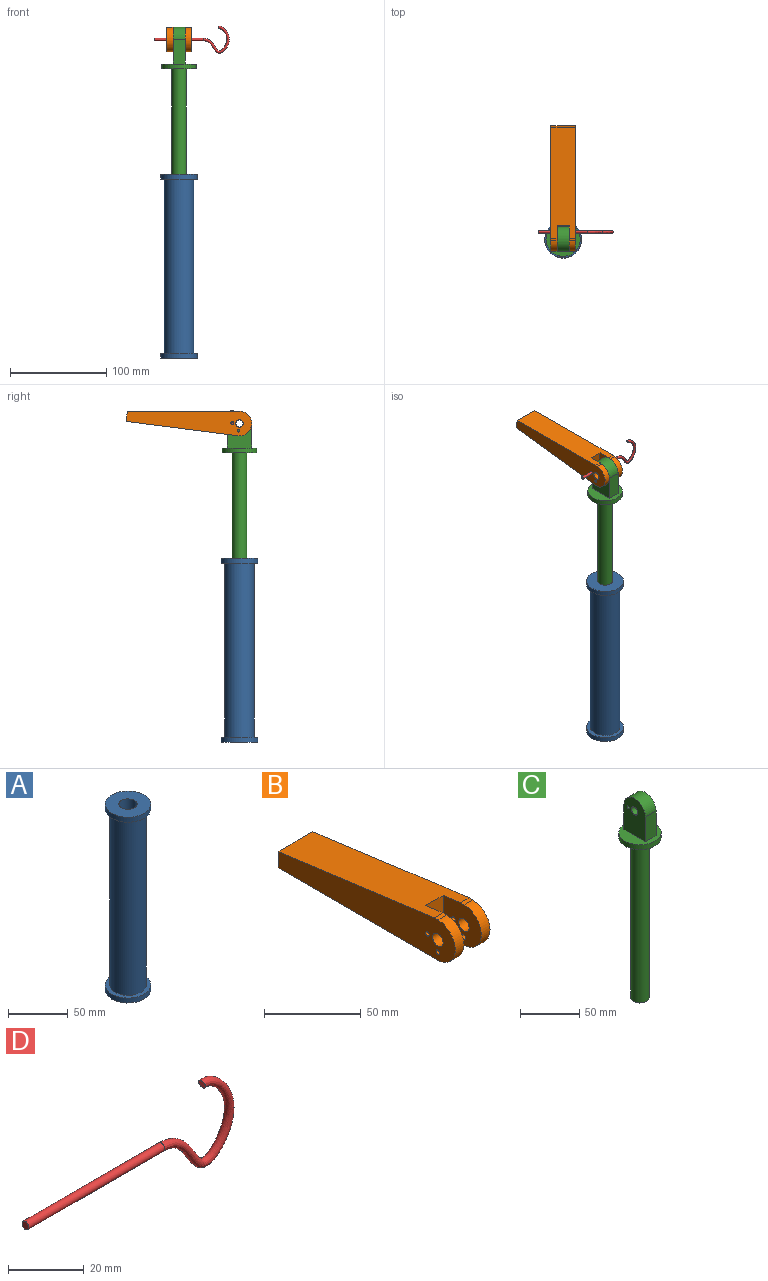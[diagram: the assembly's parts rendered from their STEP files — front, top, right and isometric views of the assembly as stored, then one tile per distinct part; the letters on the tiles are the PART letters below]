
ASSEMBLY  parts=4 mates=3
PART A: 9 faces, bbox 38.1x38.1x190.5 mm
  f0: plane 38.1x38.1mm, normal (0,0,1), area 957.7mm2, adj f1,f8
  f1: cylinder r=7.62mm len=177.8mm, axis (0,0,-1), area 8512.7mm2, adj f0,f2
  f2: plane 15.24x15.24mm, normal (0,0,1), area 182.4mm2, adj f1
  f3: plane 38.1x38.1mm, normal (0,0,-1), area 1140.1mm2, adj f4
  f4: cylinder r=19.05mm len=38.1mm, axis (0,0,-1), area 608mm2, adj f3,f5
  f5: plane 38.1x38.1mm, normal (0,0,1), area 410.4mm2, adj f4,f6
  f6: cylinder r=15.24mm len=180.34mm, axis (0,0,-1), area 17268.6mm2, adj f5,f7
  f7: plane 38.1x38.1mm, normal (0,0,-1), area 410.4mm2, adj f6,f8
  f8: cylinder r=19.05mm len=38.1mm, axis (0,0,-1), area 608mm2, adj f0,f7
PART B: 18 faces, bbox 25.4x129.5x25.4 mm
  f0: plane 6.35x2.54mm, normal (0,0,1), area 16.1mm2, adj f1,f8,f14,f16
  f1: cylinder r=12.7mm len=25.4mm, axis (-1,0,0), area 253.4mm2, adj f0,f2,f14,f16
  f2: plane 116.84x25.4mm, normal (0,0,-1), area 2774.2mm2, adj f1,f6,f7,f13,f14,f15,f16,f17
  f3: cylinder r=3.81mm len=7.62mm, axis (-1,0,0), area 152mm2, adj f14,f16
  f4: cylinder r=1.27mm len=6.35mm, axis (-1,0,0), area 50.7mm2, adj f14,f16
  f5: cylinder r=1.27mm len=6.35mm, axis (-1,0,0), area 50.7mm2, adj f14,f16
  f6: cylinder r=12.7mm len=25.4mm, axis (-1,0,0), area 253.4mm2, adj f2,f12,f13,f17
  f7: plane 25.4x10.16mm, normal (0,1,0), area 258.1mm2, adj f2,f8,f13,f14
  f8: plane 114.3x25.4mm, normal (0,0.13,0.99), area 2766.2mm2, adj f0,f7,f12,f13,f14,f15,f16,f17
  f9: cylinder r=3.81mm len=7.62mm, axis (-1,0,0), area 152mm2, adj f13,f17
  f10: cylinder r=1.27mm len=6.35mm, axis (-1,0,0), area 50.7mm2, adj f13,f17
  f11: cylinder r=1.27mm len=6.35mm, axis (-1,0,0), area 50.7mm2, adj f13,f17
  f12: plane 6.35x2.54mm, normal (0,0,1), area 16.1mm2, adj f6,f8,f13,f17
  f13: plane 129.54x25.4mm, normal (1,0,0), area 2294.4mm2, adj f2,f6,f7,f8,f9,f10,f11,f12
  f14: plane 129.54x25.4mm, normal (-1,0,0), area 2294.4mm2, adj f0,f1,f2,f3,f4,f5,f7,f8
  f15: plane 23.71x12.7mm, normal (0,-1,0), area 301.1mm2, adj f2,f8,f16,f17
  f16: plane 27.94x25.4mm, normal (1,0,0), area 574mm2, adj f0,f1,f2,f3,f4,f5,f8,f15
  f17: plane 27.94x25.4mm, normal (-1,0,0), area 574mm2, adj f2,f6,f8,f9,f10,f11,f12,f15
PART C: 12 faces, bbox 35.6x35.6x208.3 mm
  f0: plane 25.4x12.7mm, normal (0,1,0), area 322.6mm2, adj f1,f5,f6,f7
  f1: cylinder r=12.7mm len=25.4mm, axis (-1,0,0), area 506.7mm2, adj f0,f2,f5,f6
  f2: plane 25.4x12.7mm, normal (0,-1,0), area 322.6mm2, adj f1,f5,f6,f7
  f3: cylinder r=3.81mm len=12.7mm, axis (-1,0,0), area 304mm2, adj f5,f6
  f4: cylinder r=1.27mm len=12.7mm, axis (-1,0,0), area 101.3mm2, adj f5,f6
  f5: plane 38.1x25.4mm, normal (1,0,0), area 847.8mm2, adj f0,f1,f2,f3,f4,f7
  f6: plane 38.1x25.4mm, normal (-1,0,0), area 847.8mm2, adj f0,f1,f2,f3,f4,f7
  f7: plane 35.56x35.56mm, normal (0,0,1), area 670.6mm2, adj f0,f2,f5,f6,f11
  f8: plane 15.24x15.24mm, normal (0,0,-1), area 182.4mm2, adj f9
  f9: cylinder r=7.62mm len=165.1mm, axis (0,0,-1), area 7904.6mm2, adj f8,f10
  f10: plane 35.56x35.56mm, normal (0,0,-1), area 810.7mm2, adj f9,f11
  f11: cylinder r=17.78mm len=35.56mm, axis (0,0,-1), area 567.5mm2, adj f7,f10
PART D: 4 faces, bbox 77.5x5.1x28.4 mm
  f0: plane 2.54x2.48mm, normal (-0.98,0,-0.21), area 5.1mm2, adj f2
  f1: plane 2.54x2.54mm, normal (-1,0,0), area 5.1mm2, adj f3
  f2: bspline ~28.4x26.71mm, area 452.4mm2, adj f0,f3
  f3: cylinder r=1.27mm len=50.8mm, axis (-1,0,0), area 405.4mm2, adj f1,f2
PLACE A rot(axis=(0,0,-1),30.6deg) t=(0,0,-304.8)mm
PLACE B rot(axis=(1,0,0),7.3deg) t=(0,0,25.4)mm
PLACE C t=(0,0,25.4)mm
PLACE D t=(25.4,7.62,25.4)mm
MATE revolute C.f3 <-> B.f1  axis (-1,0,0) through (-6.35,0,25.4)mm
MATE cylindrical A.f1 <-> C.f9  axis (0,0,-1) through (0,0,-119.38)mm
MATE cylindrical D.f3 <-> C.f4  axis (-1,0,0) through (0,7.62,25.4)mm
